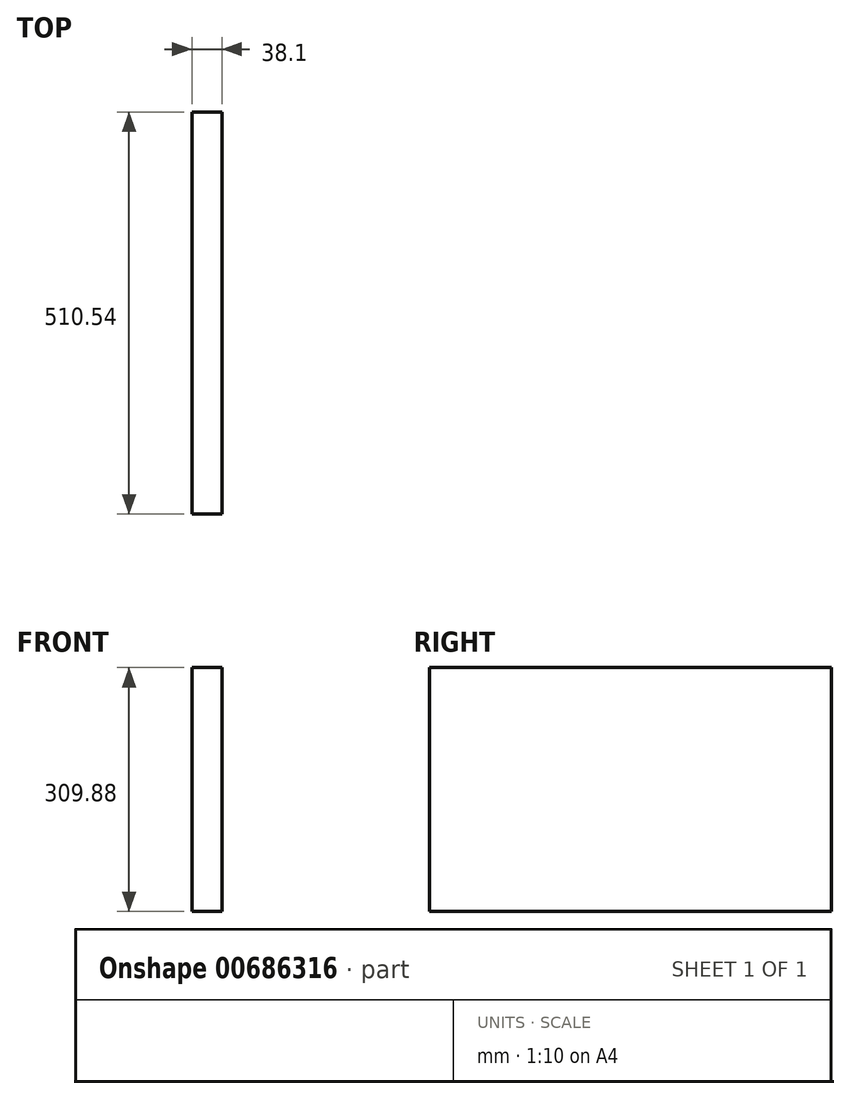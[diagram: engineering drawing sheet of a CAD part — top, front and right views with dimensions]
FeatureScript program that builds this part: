
annotation { "Feature Type Name" : "Feature", "Feature Type Description" : "" }
export const myFeature = defineFeature(function(context is Context, id is Id, definition is map)
    precondition{}
    {
        {
            var Q0;
            Q0=qCreatedBy(makeId("Right.planeOp"),FACE);
            var sketch = newSketch(context, id + "F0", { "sketchPlane" : qUnion([Q0])});
            skLineSegment(sketch, "E0.bottom", {"start": v(255.27, 154.94) * mm, "end": v(-255.27, 154.94) * mm});
            skLineSegment(sketch, "E0.top", {"start": v(255.27, -154.94) * mm, "end": v(-255.27, -154.94) * mm});
            skLineSegment(sketch, "E0.left", {"start": v(255.27, 154.94) * mm, "end": v(255.27, -154.94) * mm});
            skLineSegment(sketch, "E0.right", {"start": v(-255.27, 154.94) * mm, "end": v(-255.27, -154.94) * mm});
            skPoint(sketch, "E0.middle", {"position": v(0, 0) * mm});
            skSolve(sketch);
        }
        {
            var Q0;
            Q0=makeQuery(id+"F0.imprint","IMPRINT",FACE,{"disambiguationData":[TD([[makeQuery(id+"F0.imprint","IMPRINT",EDGE,{"derivedFrom":sQuery(id+"F0.wireOp",EDGE,"E0.bottom")}),1.0]])]});
            extrude(context, id + "F1", {"entities" : qUnion([Q0]), "depth" : 38.1 * mm, "offsetDistance" : 25.4 * mm});
        }
    });
